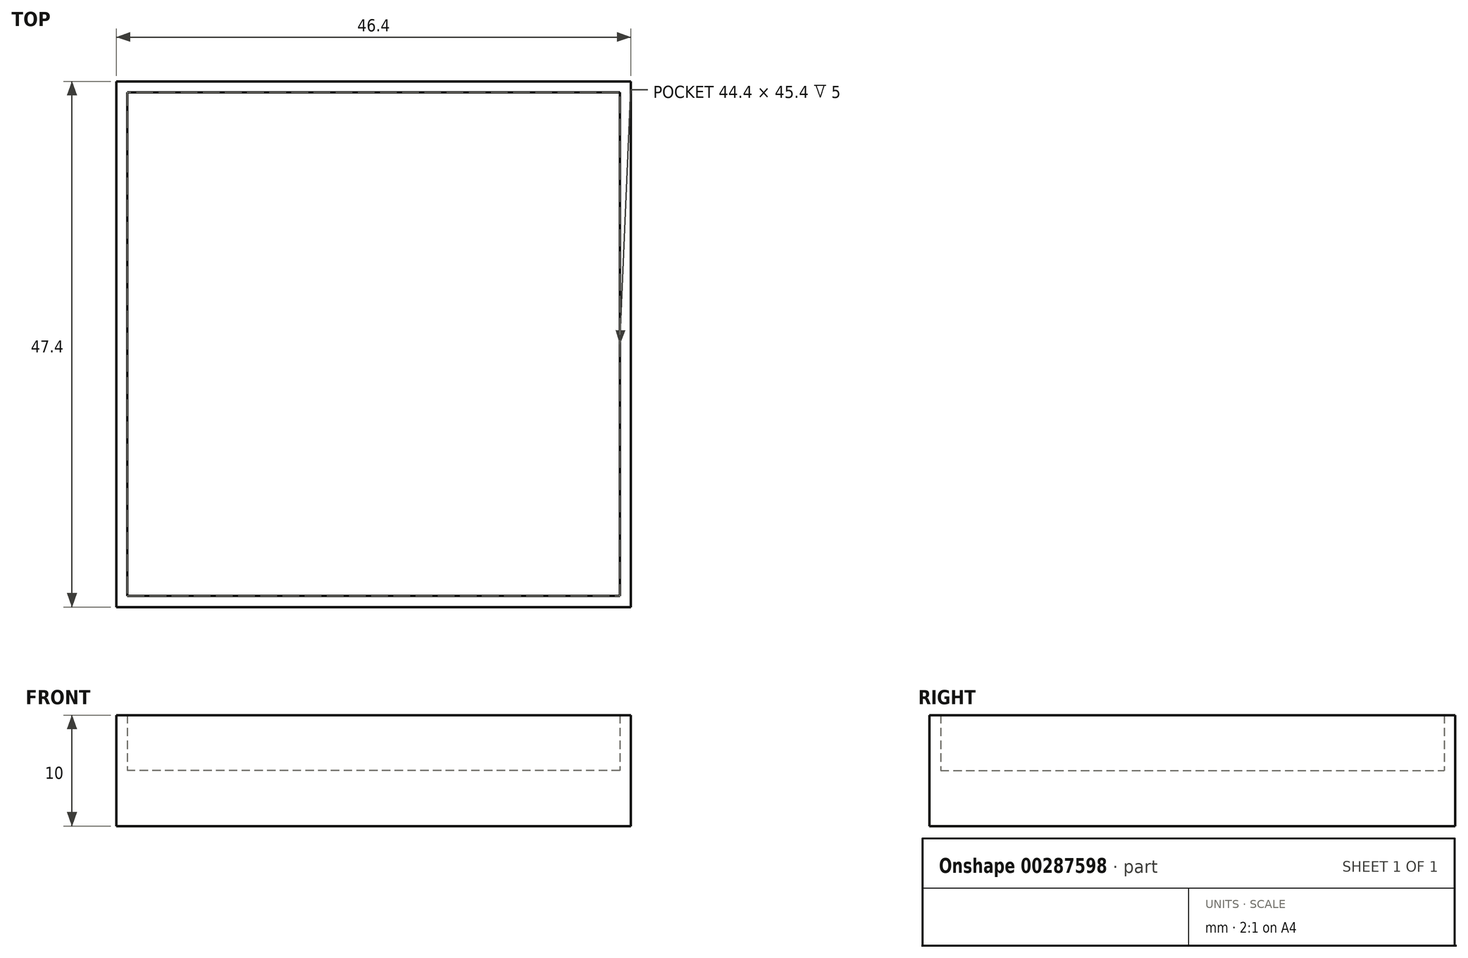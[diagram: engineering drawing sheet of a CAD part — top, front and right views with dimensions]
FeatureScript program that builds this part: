
annotation { "Feature Type Name" : "Feature", "Feature Type Description" : "" }
export const myFeature = defineFeature(function(context is Context, id is Id, definition is map)
    precondition{}
    {
        {
            var Q0;
            Q0=qCreatedBy(makeId("Top.planeOp"),FACE);
            var sketch = newSketch(context, id + "F0", { "sketchPlane" : qUnion([Q0])});
            skLineSegment(sketch, "E0.bottom", {"start": v(22.2, -22.7) * mm, "end": v(-22.2, -22.7) * mm});
            skLineSegment(sketch, "E0.top", {"start": v(22.2, 22.7) * mm, "end": v(-22.2, 22.7) * mm});
            skLineSegment(sketch, "E0.left", {"start": v(22.2, -22.7) * mm, "end": v(22.2, 22.7) * mm});
            skLineSegment(sketch, "E0.right", {"start": v(-22.2, -22.7) * mm, "end": v(-22.2, 22.7) * mm});
            skPoint(sketch, "E0.middle", {"position": v(0, 0) * mm});
            skLineSegment(sketch, "E1.bottom", {"start": v(23.2, -23.7) * mm, "end": v(-23.2, -23.7) * mm});
            skLineSegment(sketch, "E1.top", {"start": v(23.2, 23.7) * mm, "end": v(-23.2, 23.7) * mm});
            skLineSegment(sketch, "E1.left", {"start": v(23.2, -23.7) * mm, "end": v(23.2, 23.7) * mm});
            skLineSegment(sketch, "E1.right", {"start": v(-23.2, -23.7) * mm, "end": v(-23.2, 23.7) * mm});
            skSolve(sketch);
        }
        {
            var Q0;
            Q0 = qSketchRegion(id + "F0", true);
            extrude(context, id + "F1", {"entities" : qUnion([Q0]), "depth" : 10 * mm, "offsetDistance" : 25 * mm});
        }
        {
            var Q0;
            Q0=makeQuery(id+"F0.imprint","IMPRINT",FACE,{"disambiguationData":[TD([[makeQuery(id+"F0.imprint","IMPRINT",EDGE,{"derivedFrom":sQuery(id+"F0.wireOp",EDGE,"E0.bottom")}),-1.0]])]});
            extrude(context, id + "F2", {"entities" : qUnion([Q0]), "operationType" : NewBodyOperationType.ADD, "depth" : 5 * mm, "offsetDistance" : 25 * mm});
        }
    });
